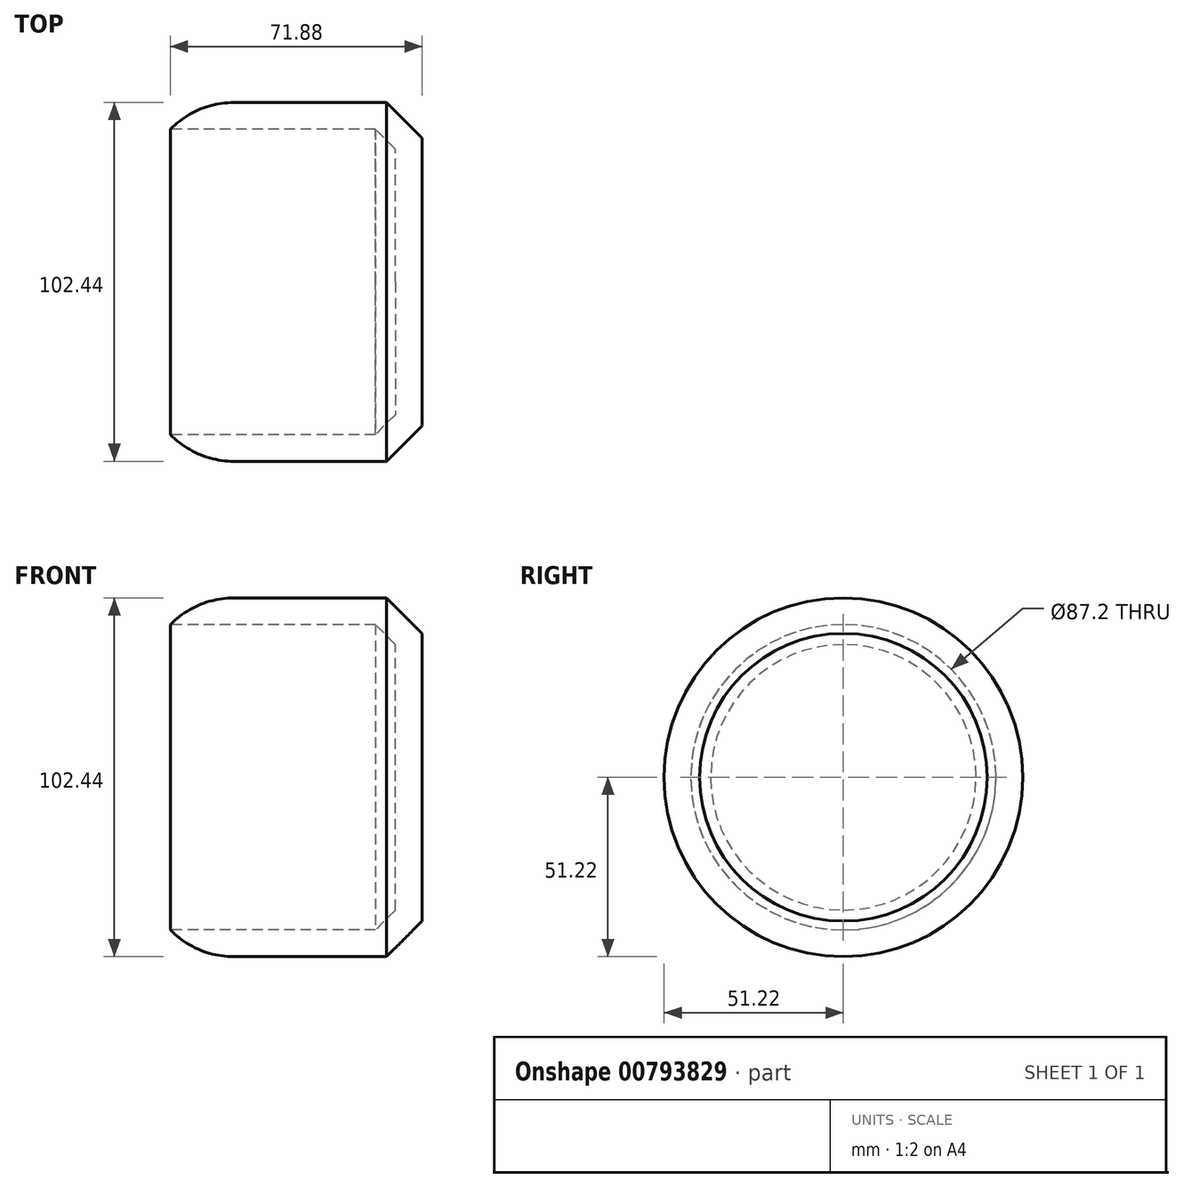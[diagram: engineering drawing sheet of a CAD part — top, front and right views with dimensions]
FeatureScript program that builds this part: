
annotation { "Feature Type Name" : "Feature", "Feature Type Description" : "" }
export const myFeature = defineFeature(function(context is Context, id is Id, definition is map)
    precondition{}
    {
        {
            var Q0;
            Q0=qCreatedBy(makeId("Right.planeOp"),FACE);
            var sketch = newSketch(context, id + "F0", { "sketchPlane" : qUnion([Q0])});
            skCircle(sketch, "E0", {"center": v(0, 0) * mm, "radius": 51.22 * mm});
            skSolve(sketch);
        }
        {
            var Q0;
            Q0=makeQuery(id+"F0.imprint","IMPRINT",FACE,{"disambiguationData":[TD([[makeQuery(id+"F0.imprint","IMPRINT",EDGE,{"derivedFrom":sQuery(id+"F0.wireOp",EDGE,"E0")}),1.0]])]});
            extrude(context, id + "F1", {"entities" : qUnion([Q0]), "depth" : 71.88 * mm, "offsetDistance" : 25.4 * mm});
        }
        {
            var Q0;
            Q0=makeQuery(id+"F1.opExtrude","CAP_EDGE",EDGE,{"disambiguationData":[OSD([sQuery(id+"F0.wireOp",EDGE,"E0")])],"isStart":false});
            chamfer(context, id + "F2", {"entities" : qUnion([Q0]), "width" : 10.16 * mm, "tangentPropagation" : true});
        }
        {
            var Q0;
            Q0=makeQuery(id+"F1.opExtrude","CAP_FACE",FACE,{"disambiguationData":[OSD([sQuery(id+"F0.wireOp",EDGE,"E0")])],"isStart":true});
            shell(context, id + "F3", {"entities" : qUnion([Q0]), "thickness" : 7.62 * mm});
        }
        {
            var Q0;
            Q0=makeQuery(id+"F1.opExtrude","CAP_EDGE",EDGE,{"disambiguationData":[OSD([sQuery(id+"F0.wireOp",EDGE,"E0")])],"isStart":true});
            fillet(context, id + "F4", {"entities" : qUnion([Q0]), "radius" : 25.4 * mm, "tangentPropagation" : true, "allowEdgeOverflow" : false});
        }
    });
